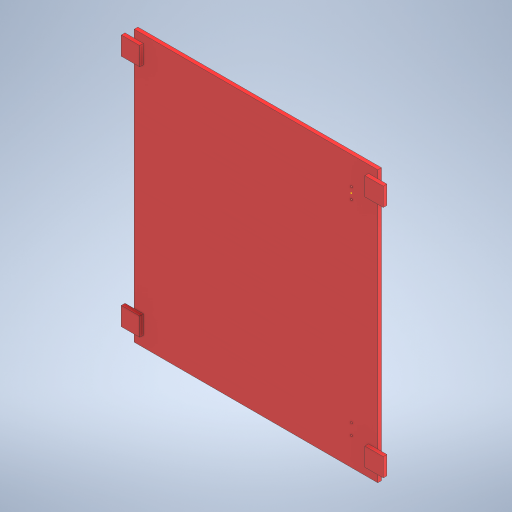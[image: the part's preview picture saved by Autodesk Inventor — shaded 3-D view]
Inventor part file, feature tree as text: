
AUTODESK INVENTOR PART (.ipt)
format: ipt  version: 2023.2 (Build 272271030, 271C)  size: 296,960 bytes
history: native  units: mm
features: reference x10, other x8, sheet_metal_op x3, sketch x2, projected_geometry x1
ambient origin geometry x8: Origin, YZ Plane, XZ Plane, XY Plane, X Axis, Y Axis, Z Axis, Center Point
bodies: Solid1 (feature_tree)
feature tree (24):
  sheet_metal_op  "Face1"
  sketch  "Sketch2"  dims[d3=5.1mm d4=10.0mm d5=50.0mm d6=10.0mm d7=10.0mm d8=5.0mm d9=20.0mm d10=10.0mm d11=635.799mm d12=635.799mm d13=317.8995mm]
  sheet_metal_op  "Face2"
  sketch  "Sketch1"  dims[d0=735.799256mm]
  reference  "Reference1"
  reference  "Reference2"
  reference  "Reference3"
  reference  "Reference4"
  reference  "Reference5"
  reference  "Reference6"
  reference  "Reference7"
  reference  "Reference8"
  reference  "Reference9"
  reference  "Reference10"
  other  "Plate1"
  other  "Plate2"
  sheet_metal_op  "Bend1"
  projected_geometry  "Projected Loop1"
  other  "ensamble_general.iam"
  other  "soporte1:1"
  other  "AISC (L 1 x 1 x 1/8) - 28.968:2"
  other  "AISC (L 1 x 1 x 1/8) - 28.968:1"
  other  "sujetador:1"
  other  "sujetador_MIR:1"
